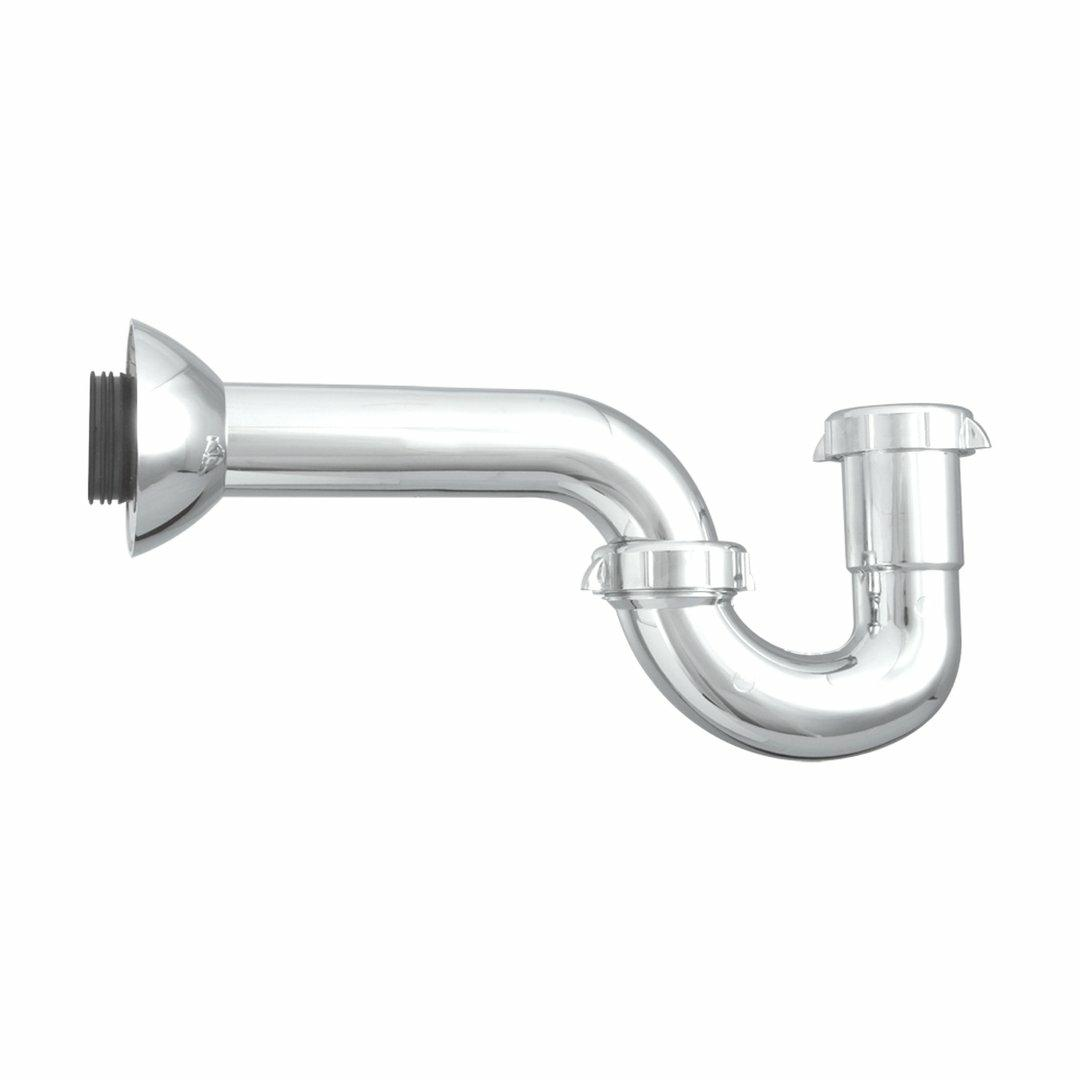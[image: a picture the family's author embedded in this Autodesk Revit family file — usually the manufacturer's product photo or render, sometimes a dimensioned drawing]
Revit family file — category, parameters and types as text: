
# Revit family: BIM_01-31704-11
name_source: partatom
category: Aparatos sanitarios
units: mm (PartAtom-declared; Revit-internal decimal feet)

## family parameters
Activar corte en vistas = No
Anfitrión = Cara
Compartido = No
Corte con vacíos al cargar = No
Cota de conector redondo = Usar diámetro
Mantener orientación de anotación = No
Número OmniClass = 23.31.11.00
Punto de cálculo de habitación = No
Tipo de pieza = Normal

## types (1)
- 01-31704-11
    Alto = 175 mm
    Ancho = 430 mm  [stored 1.41076 ft]
    Conexiones = 43 cm largo X 43Cm Ancho, 17.5 Cm Profundidad
    Conexión AC = Sí
    Conexión AF = Sí
    Conexión de residuos = No
    Conexión de ventilación = No
    Date Modified = 08-08-2025
    Descripción = Lavaplatos en acero
    Elevación por defecto = 0 mm  [stored 0 ft]
    Fabricante = Gricol
    Garantia Especifica = 5 años
    Imagen de tipo = LAVAPLATOS EN ACERO POCETA 43 x 43 cm.PNG
    Largo = 430 mm  [stored 1.41076 ft]
    Link Ficha Tecnica = https://infotecnica.gricol.com
    Material = Acero inoxidable
    Material Principal = Acero inoxidable
    Modelo = 01-31704-11
    Peso = 2.50 kg
    Product Name = Lavaplatos De Submontar 43 X 43 Cm Con Complementos
    Resistencia a Corrosión = Si
    Sitio web = https://www.gricol.com
    Tipo de Uso = Residencial y/o Institucional
    URL = https://www.gricol.com

note: [stored X ft] marks values corroborated as IEEE doubles in the binary element streams (Revit-internal decimal feet)

## geometry (parser evidence)
native form markers: Blend x2, Sweep x15
no freeform markers — native parametric forms only
